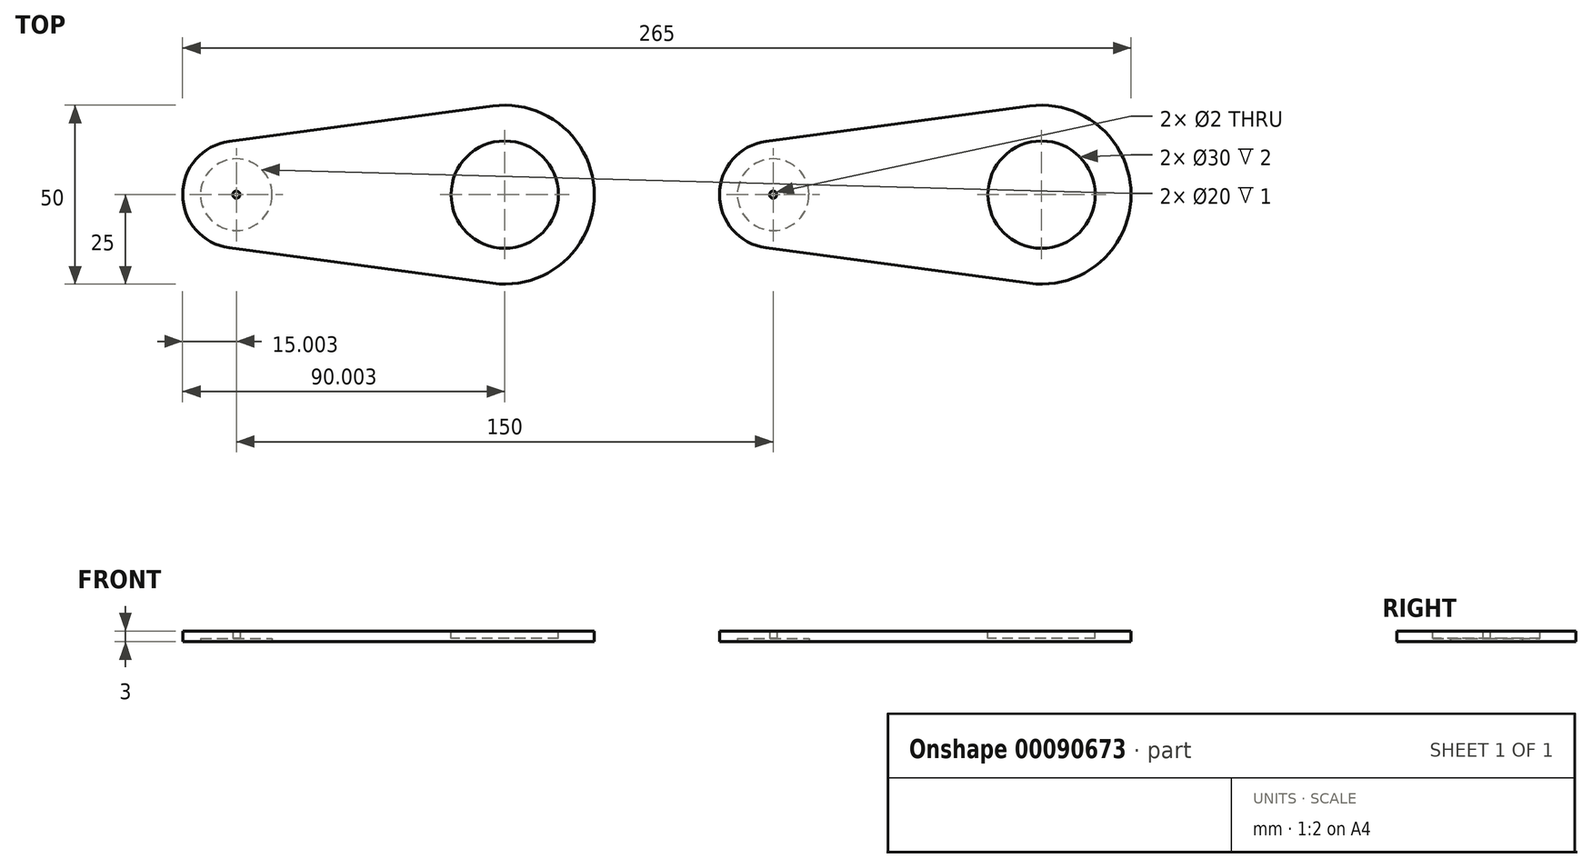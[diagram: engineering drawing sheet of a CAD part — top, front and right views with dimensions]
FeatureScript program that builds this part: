
annotation { "Feature Type Name" : "Feature", "Feature Type Description" : "" }
export const myFeature = defineFeature(function(context is Context, id is Id, definition is map)
    precondition{}
    {
        {
            var Q0;
            Q0=qCreatedBy(makeId("Top.planeOp"),FACE);
            var sketch = newSketch(context, id + "F0", { "sketchPlane" : qUnion([Q0])});
            skCircle(sketch, "E0", {"center": v(-7.24, 0) * mm, "radius": 1 * mm});
            skCircle(sketch, "E1", {"center": v(-7.24, 0) * mm, "radius": 15 * mm});
            skCircle(sketch, "E2", {"center": v(67.76, 0) * mm, "radius": 25 * mm});
            skLineSegment(sketch, "E3", {"start": v(-9.24, 14.87) * mm, "end": v(67.8, 25.23) * mm});
            skLineSegment(sketch, "E4", {"start": v(-9.24, -14.87) * mm, "end": v(64.43, -24.78) * mm});
            skSolve(sketch);
        }
        {
            var Q0;
            Q0=makeQuery(id+"F0.imprint","IMPRINT",FACE,{"disambiguationData":[TD([[makeQuery(id+"F0.imprint","IMPRINT",EDGE,{"derivedFrom":sQuery(id+"F0.wireOp",EDGE,"E0")}),-1.0]])]});
            var Q1;
            {var subQ3=sQuery(id+"F0.wireOp",EDGE,"E4");Q1=makeQuery(id+"F0.imprint","IMPRINT",FACE,{"disambiguationData":[TD([[makeQuery(id+"F0.imprint","IMPRINT",EDGE,{"derivedFrom":subQ3}),1.0]])]});}
            var Q2;
            {var subQ0=sQuery(id+"F0.wireOp",EDGE,"E2");var subQ1=makeQuery(id+"F0.imprint","INTERSECT",VERTEX,{"derivedFrom":[subQ0,sQuery(id+"F0.wireOp",EDGE,"E4")]});Q2=makeQuery(id+"F0.imprint","IMPRINT",FACE,{"disambiguationData":[TD([[makeQuery(id+"F0.imprint","IMPRINT",EDGE,{"disambiguationData":[TD([[subQ1,1.0]])],"derivedFrom":subQ0}),1.0]])]});}
            extrude(context, id + "F1", {"entities" : qUnion([Q0, Q1, Q2]), "depth" : 25 * mm});
        }
        {
            var Q0;
            Q0=makeQuery(id+"F1.opExtrude","CAP_FACE",FACE,{"disambiguationData":[OSD([sQuery(id+"F0.wireOp",EDGE,"E0"),sQuery(id+"F0.wireOp",EDGE,"E1"),sQuery(id+"F0.wireOp",EDGE,"E2"),sQuery(id+"F0.wireOp",EDGE,"E3"),sQuery(id+"F0.wireOp",EDGE,"E4")])],"isStart":false});
            extrude(context, id + "F2", {"entities" : qUnion([Q0]), "operationType" : NewBodyOperationType.REMOVE, "oppositeDirection" : true, "depth" : 20 * mm});
        }
        {
            var Q0;
            Q0=makeQuery(id+"F2.boolean.opBoolean","COPY",FACE,{"derivedFrom":makeQuery(id+"F2.opExtrude","CAP_FACE",FACE,{"disambiguationData":[OSD([sQuery(id+"F0.wireOp",EDGE,"E0"),sQuery(id+"F0.wireOp",EDGE,"E1"),sQuery(id+"F0.wireOp",EDGE,"E2"),sQuery(id+"F0.wireOp",EDGE,"E3"),sQuery(id+"F0.wireOp",EDGE,"E4")])],"isStart":false})});
            extrude(context, id + "F3", {"entities" : qUnion([Q0]), "operationType" : NewBodyOperationType.REMOVE, "oppositeDirection" : true, "depth" : 1 * mm});
        }
        {
            var Q0;
            Q0=makeQuery(id+"F3.boolean.opBoolean","COPY",FACE,{"derivedFrom":makeQuery(id+"F3.opExtrude","CAP_FACE",FACE,{"disambiguationData":[OSD([sQuery(id+"F0.wireOp",EDGE,"E0"),sQuery(id+"F0.wireOp",EDGE,"E1"),sQuery(id+"F0.wireOp",EDGE,"E2"),sQuery(id+"F0.wireOp",EDGE,"E3"),sQuery(id+"F0.wireOp",EDGE,"E4")])],"isStart":false})});
            extrude(context, id + "F4", {"entities" : qUnion([Q0]), "operationType" : NewBodyOperationType.REMOVE, "oppositeDirection" : true, "depth" : 1 * mm});
        }
        {
            var Q0;
            Q0=makeQuery(id+"F4.boolean.opBoolean","COPY",FACE,{"derivedFrom":makeQuery(id+"F4.opExtrude","CAP_FACE",FACE,{"disambiguationData":[OSD([sQuery(id+"F0.wireOp",EDGE,"E0"),sQuery(id+"F0.wireOp",EDGE,"E1"),sQuery(id+"F0.wireOp",EDGE,"E2"),sQuery(id+"F0.wireOp",EDGE,"E3"),sQuery(id+"F0.wireOp",EDGE,"E4")])],"isStart":false})});
            var sketch = newSketch(context, id + "F5", { "sketchPlane" : qUnion([Q0])});
            skCircle(sketch, "E5", {"center": v(67.76, 0) * mm, "radius": 15 * mm});
            skSolve(sketch);
        }
        {
            var Q0;
            Q0=makeQuery(id+"F5.imprint","IMPRINT",FACE,{"disambiguationData":[TD([[makeQuery(id+"F5.imprint","IMPRINT",EDGE,{"derivedFrom":sQuery(id+"F5.wireOp",EDGE,"E5")}),1.0]])]});
            extrude(context, id + "F6", {"entities" : qUnion([Q0]), "operationType" : NewBodyOperationType.REMOVE, "oppositeDirection" : true, "depth" : 2 * mm});
        }
        {
            var Q0;
            Q0=makeQuery(id+"F1.opExtrude","CAP_FACE",FACE,{"disambiguationData":[OSD([sQuery(id+"F0.wireOp",EDGE,"E0"),sQuery(id+"F0.wireOp",EDGE,"E1"),sQuery(id+"F0.wireOp",EDGE,"E2"),sQuery(id+"F0.wireOp",EDGE,"E3"),sQuery(id+"F0.wireOp",EDGE,"E4")])],"isStart":true});
            var sketch = newSketch(context, id + "F7", { "sketchPlane" : qUnion([Q0])});
            skCircle(sketch, "E6", {"center": v(-7.24, 0) * mm, "radius": 10 * mm});
            skSolve(sketch);
        }
        {
            var Q0;
            Q0=makeQuery(id+"F7.imprint","IMPRINT",FACE,{"disambiguationData":[TD([[makeQuery(id+"F7.imprint","IMPRINT",EDGE,{"derivedFrom":sQuery(id+"F7.wireOp",EDGE,"E6")}),1.0]])]});
            extrude(context, id + "F8", {"entities" : qUnion([Q0]), "operationType" : NewBodyOperationType.REMOVE, "oppositeDirection" : true, "depth" : 1 * mm});
        }
        {
            var Q0;
            Q0=makeQuery(id+"F1.opExtrude","SWEPT_BODY",BODY,{"disambiguationData":[OSD([sQuery(id+"F0.wireOp",EDGE,"E0"),sQuery(id+"F0.wireOp",EDGE,"E1"),sQuery(id+"F0.wireOp",EDGE,"E2"),sQuery(id+"F0.wireOp",EDGE,"E3"),sQuery(id+"F0.wireOp",EDGE,"E4")])]});
            transform(context, id + "F9", {"entities" : qUnion([Q0]), "transformType" : TransformType.TRANSLATION_3D, "dx" : 150 * mm, "dy" : 0 * mm, "dz" : 0 * mm, "makeCopy" : true});
        }
    });
